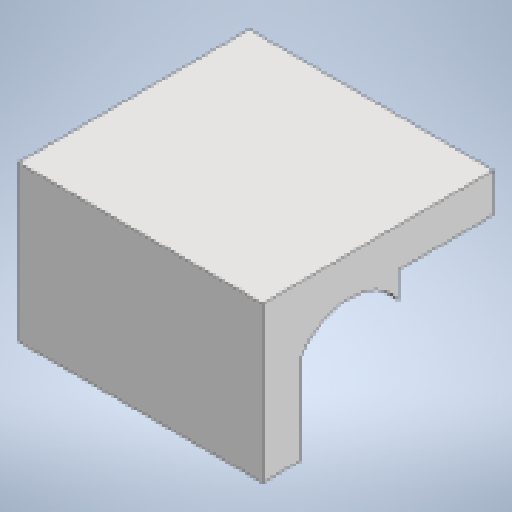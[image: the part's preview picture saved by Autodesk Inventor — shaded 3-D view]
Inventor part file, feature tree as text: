
AUTODESK INVENTOR PART (.ipt)
format: ipt  version: 2023.5 (Build 275446000, 446)  size: 367,616 bytes
history: native  units: mm
features: extrude x12, sketch x12, reference x11, other x10, projected_geometry x6, fillet x1
ambient origin geometry x8: Origin, YZ Plane, XZ Plane, XY Plane, X Axis, Y Axis, Z Axis, Center Point
bodies: Body1 (feature_tree)
feature tree (52):
  other  "Bryła1"
  extrude  "Wyciągnięcie proste1"  Depth=12.0mm
  extrude  "Wyciągnięcie proste2"  Depth=10.0mm
  sketch  "Szkic3"
  other  "Płaszczyzna konstrukcyjna1"
  extrude  "Wyciągnięcie proste3"  Depth=4.0mm
  sketch  "Szkic4"
  other  "Płaszczyzna konstrukcyjna2"
  extrude  "Wyciągnięcie proste4"  Depth=9.0mm TaperAngle=0.0deg
  sketch  "Szkic5"
  other  "Płaszczyzna konstrukcyjna3"
  extrude  "Wyciągnięcie proste5"  Depth=9.0mm TaperAngle=0.0deg
  extrude  "Wyciągnięcie proste6"  Depth=10.0mm TaperAngle=0.0deg
  extrude  "Wyciągnięcie proste7"  Depth=10.0mm TaperAngle=0.0deg
  fillet  "Zaokrąglenie1"  Radius=10.0mm
  sketch  "Szkic8"
  other  "Płaszczyzna konstrukcyjna4"
  extrude  "Wyciągnięcie proste8"  Depth=0.2mm
  extrude  "Wyciągnięcie proste9"  Depth=2.0mm
  extrude  "Wyciągnięcie proste10"  Depth=1.0mm TaperAngle=0.0deg
  extrude  "Wyciągnięcie proste11"  Depth=2.0mm
  extrude  "Wyciągnięcie proste12"  Depth=8.0mm TaperAngle=0.0deg
  sketch  "Szkic1"
  sketch  "Szkic2"
  reference  "Odniesienie1"
  reference  "Odniesienie2"
  projected_geometry  "Pętla rzutowana1"
  reference  "Odniesienie3"
  reference  "Odniesienie4"
  projected_geometry  "Pętla rzutowana2"
  reference  "Odniesienie5"
  projected_geometry  "Pętla rzutowana3"
  sketch  "Szkic6"
  reference  "Odniesienie6"
  reference  "Odniesienie7"
  reference  "Odniesienie8"
  reference  "Odniesienie9"
  sketch  "Szkic7"
  projected_geometry  "Pętla rzutowana4"
  projected_geometry  "Pętla rzutowana5"
  sketch  "Szkic9"
  reference  "Odniesienie10"
  sketch  "Szkic10"
  reference  "Odniesienie11"
  projected_geometry  "Pętla rzutowana6"
  sketch  "Szkic11"
  sketch  "Szkic12"
  other  "Zespół4"
  other  "silnik:2"
  other  "silnik:1"
  other  "lipo-300:1"
  other  "mocowanie:1"
